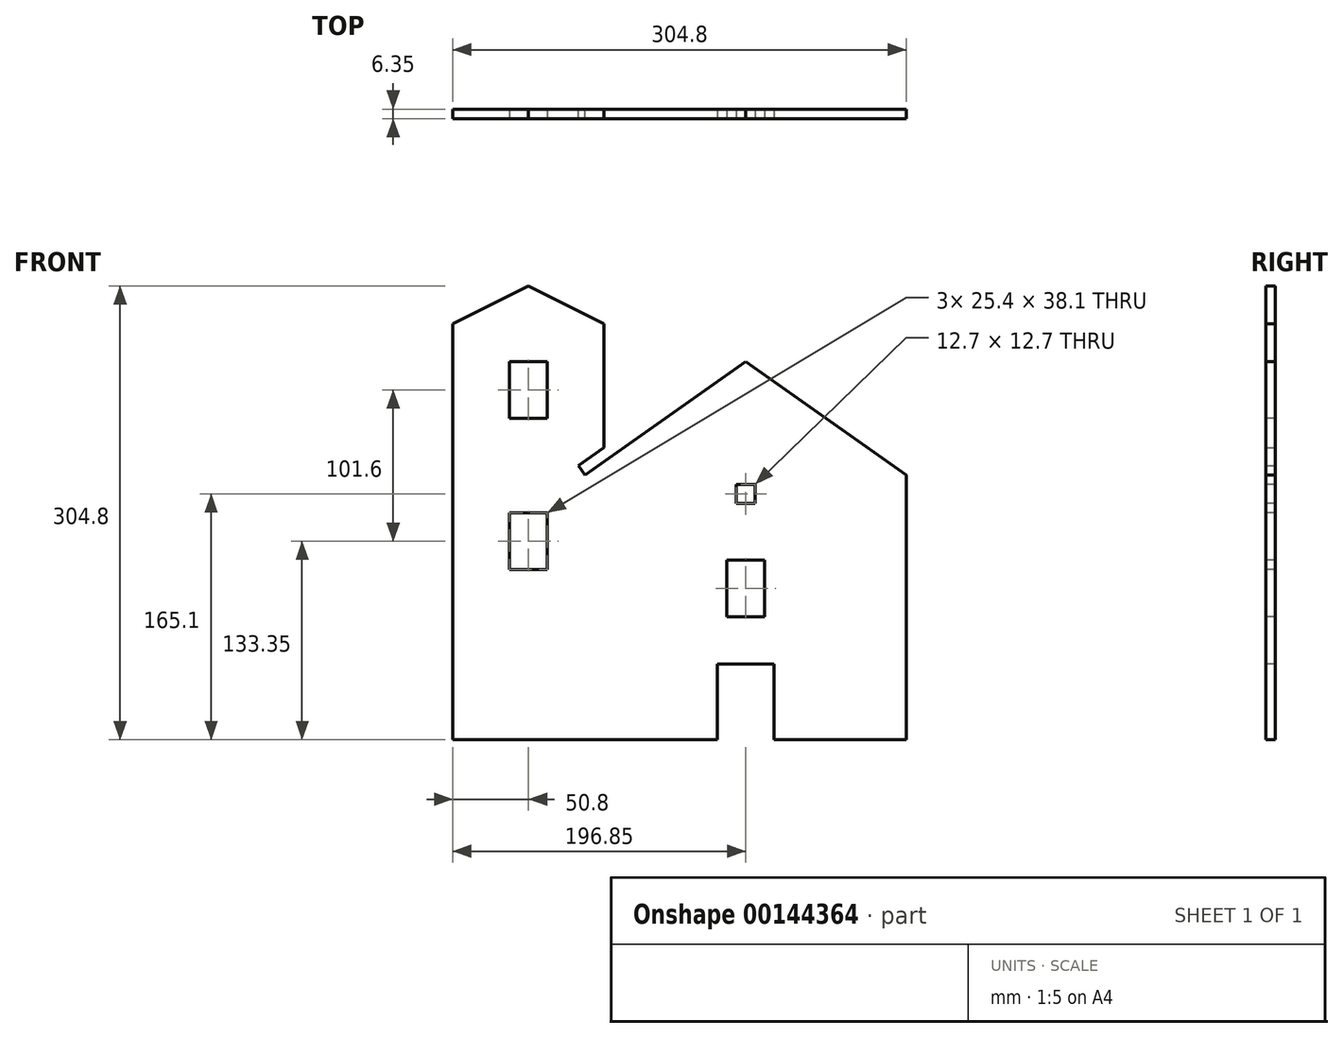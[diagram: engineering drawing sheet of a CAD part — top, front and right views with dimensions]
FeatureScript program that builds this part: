
annotation { "Feature Type Name" : "Feature", "Feature Type Description" : "" }
export const myFeature = defineFeature(function(context is Context, id is Id, definition is map)
    precondition{}
    {
        {
            var Q0;
            Q0=qCreatedBy(makeId("Front.planeOp"),FACE);
            var sketch = newSketch(context, id + "F0", { "sketchPlane" : qUnion([Q0])});
            skLineSegment(sketch, "E0", {"start": v(0, 0) * mm, "end": v(0, 279.4) * mm});
            skLineSegment(sketch, "E1", {"start": v(0, 279.4) * mm, "end": v(101.6, 279.4) * mm, "construction": true});
            skLineSegment(sketch, "E2", {"start": v(101.6, 279.4) * mm, "end": v(101.6, 196.1) * mm});
            skLineSegment(sketch, "E3", {"start": v(196.85, 254) * mm, "end": v(304.8, 177.8) * mm});
            skLineSegment(sketch, "E4", {"start": v(304.8, 177.8) * mm, "end": v(304.8, 0) * mm});
            skLineSegment(sketch, "E5", {"start": v(304.8, 0) * mm, "end": v(0, 0) * mm});
            skLineSegment(sketch, "E6", {"start": v(88.9, 177.8) * mm, "end": v(84.5, 184.03) * mm});
            skLineSegment(sketch, "E7", {"start": v(84.5, 184.03) * mm, "end": v(101.6, 196.1) * mm});
            skLineSegment(sketch, "E8", {"start": v(88.9, 177.8) * mm, "end": v(196.85, 254) * mm});
            skLineSegment(sketch, "E9", {"start": v(88.9, 177.8) * mm, "end": v(304.8, 177.8) * mm, "construction": true});
            skLineSegment(sketch, "E10", {"start": v(196.85, 177.8) * mm, "end": v(196.85, 254) * mm, "construction": true});
            skLineSegment(sketch, "E11", {"start": v(0, 279.4) * mm, "end": v(50.8, 304.8) * mm});
            skLineSegment(sketch, "E12", {"start": v(50.8, 304.8) * mm, "end": v(101.6, 279.4) * mm});
            skLineSegment(sketch, "E13", {"start": v(50.8, 304.8) * mm, "end": v(50.8, 279.4) * mm, "construction": true});
            skSolve(sketch);
        }
        {
            var Q0;
            Q0=makeQuery(id+"F0.imprint","IMPRINT",FACE,{"disambiguationData":[TD([[makeQuery(id+"F0.imprint","IMPRINT",EDGE,{"derivedFrom":sQuery(id+"F0.wireOp",EDGE,"E0")}),-1.0]])]});
            extrude(context, id + "F1", {"entities" : qUnion([Q0]), "depth" : 6.35 * mm});
        }
        {
            var Q0;
            Q0=makeQuery(id+"F1.opExtrude","CAP_FACE",FACE,{"disambiguationData":[OSD([sQuery(id+"F0.wireOp",EDGE,"E0"),sQuery(id+"F0.wireOp",EDGE,"E1"),sQuery(id+"F0.wireOp",EDGE,"E2"),sQuery(id+"F0.wireOp",EDGE,"E3"),sQuery(id+"F0.wireOp",EDGE,"E4"),sQuery(id+"F0.wireOp",EDGE,"E5"),sQuery(id+"F0.wireOp",EDGE,"E6"),sQuery(id+"F0.wireOp",EDGE,"E7"),sQuery(id+"F0.wireOp",EDGE,"E8")])],"isStart":false});
            var sketch = newSketch(context, id + "F2", { "sketchPlane" : qUnion([Q0])});
            skLineSegment(sketch, "E14.bottom", {"start": v(63.5, 215.9) * mm, "end": v(38.1, 215.9) * mm});
            skLineSegment(sketch, "E14.top", {"start": v(63.5, 254) * mm, "end": v(38.1, 254) * mm});
            skLineSegment(sketch, "E14.left", {"start": v(63.5, 215.9) * mm, "end": v(63.5, 254) * mm});
            skLineSegment(sketch, "E14.right", {"start": v(38.1, 215.9) * mm, "end": v(38.1, 254) * mm});
            skPoint(sketch, "E14.middle", {"position": v(50.8, 234.95) * mm});
            skLineSegment(sketch, "E15.bottom", {"start": v(63.5, 114.3) * mm, "end": v(38.1, 114.3) * mm});
            skLineSegment(sketch, "E15.top", {"start": v(63.5, 152.4) * mm, "end": v(38.1, 152.4) * mm});
            skLineSegment(sketch, "E15.left", {"start": v(63.5, 114.3) * mm, "end": v(63.5, 152.4) * mm});
            skLineSegment(sketch, "E15.right", {"start": v(38.1, 114.3) * mm, "end": v(38.1, 152.4) * mm});
            skPoint(sketch, "E15.middle", {"position": v(50.8, 133.35) * mm});
            skLineSegment(sketch, "E16.bottom", {"start": v(209.55, 82.55) * mm, "end": v(184.15, 82.55) * mm});
            skLineSegment(sketch, "E16.top", {"start": v(209.55, 120.65) * mm, "end": v(184.15, 120.65) * mm});
            skLineSegment(sketch, "E16.left", {"start": v(209.55, 82.55) * mm, "end": v(209.55, 120.65) * mm});
            skLineSegment(sketch, "E16.right", {"start": v(184.15, 82.55) * mm, "end": v(184.15, 120.65) * mm});
            skPoint(sketch, "E16.middle", {"position": v(196.85, 101.6) * mm});
            skLineSegment(sketch, "E17", {"start": v(50.8, 279.4) * mm, "end": v(50.8, 0) * mm, "construction": true});
            skLineSegment(sketch, "E18", {"start": v(196.85, 177.8) * mm, "end": v(196.85, 0) * mm, "construction": true});
            skLineSegment(sketch, "E19.bottom", {"start": v(177.8, 0) * mm, "end": v(215.9, 0) * mm});
            skLineSegment(sketch, "E19.top", {"start": v(177.8, 50.8) * mm, "end": v(215.9, 50.8) * mm});
            skLineSegment(sketch, "E19.left", {"start": v(177.8, 0) * mm, "end": v(177.8, 50.8) * mm});
            skLineSegment(sketch, "E19.right", {"start": v(215.9, 0) * mm, "end": v(215.9, 50.8) * mm});
            skPoint(sketch, "E19.middle", {"position": v(196.85, 25.4) * mm});
            skLineSegment(sketch, "E20.bottom", {"start": v(190.5, 158.75) * mm, "end": v(203.2, 158.75) * mm});
            skLineSegment(sketch, "E20.top", {"start": v(190.5, 171.45) * mm, "end": v(203.2, 171.45) * mm});
            skLineSegment(sketch, "E20.left", {"start": v(190.5, 158.75) * mm, "end": v(190.5, 171.45) * mm});
            skLineSegment(sketch, "E20.right", {"start": v(203.2, 158.75) * mm, "end": v(203.2, 171.45) * mm});
            skPoint(sketch, "E20.middle", {"position": v(196.85, 165.1) * mm});
            skSolve(sketch);
        }
        {
            var Q0;
            Q0 = qSketchRegion(id + "F2", true);
            extrude(context, id + "F3", {"entities" : qUnion([Q0]), "operationType" : NewBodyOperationType.REMOVE, "endBound" : BoundingType.THROUGH_ALL, "oppositeDirection" : true, "depth" : 25.4 * mm});
        }
    });
